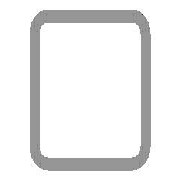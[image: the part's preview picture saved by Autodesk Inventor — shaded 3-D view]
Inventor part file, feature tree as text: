
AUTODESK INVENTOR PART (.ipt)
format: ipt  version: 2025.1 (Build 291241020, 241B)  size: 166,912 bytes
history: native  units: mm (DEFAULTED — no unit token found)
features: other x3, sketch x3, projected_geometry x2, extrude x1, plane x1
ambient origin geometry x8: Origin, YZ Plane, XZ Plane, XY Plane, X Axis, Y Axis, Z Axis, Center Point
bodies: Solid1 (feature_tree), Body (feature_tree)
feature tree (10):
  other  "Driven Length"
  other  "Start plane"
  other  "End plane"
  sketch  "Sketch5"  dims[d7=6.0mm]
  extrude  "Extrusion2"  TaperAngle=0.0deg  [1 undecoded]
  sketch  "Sketch3"  dims[d3=1000.0mm d4=0.0mm]
  plane  "Work Plane3"
  sketch  "Sketch6"  dims[d9=80.0mm d11=80.0mm d12=3.0mm d13=-0.0mm d14=1000.0mm d15=40.0mm d16=40.0mm d17=90.0deg d18=1000.0mm d22=450.0mm d24=1200.0mm d25=114.0mm d26=40.0mm d27=1200.0mm d28=310.0mm d30=397.570227mm d31=0.0mm d32=0.0mm d33=10.0mm]
  projected_geometry  "Projected Loop1"
  projected_geometry  "Projected Loop2"
note: 1 required parameter value undecoded (feature->parameter linkage not recoverable at this tier; creation-order binding heuristic only, values carry confidence <= 0.55)
